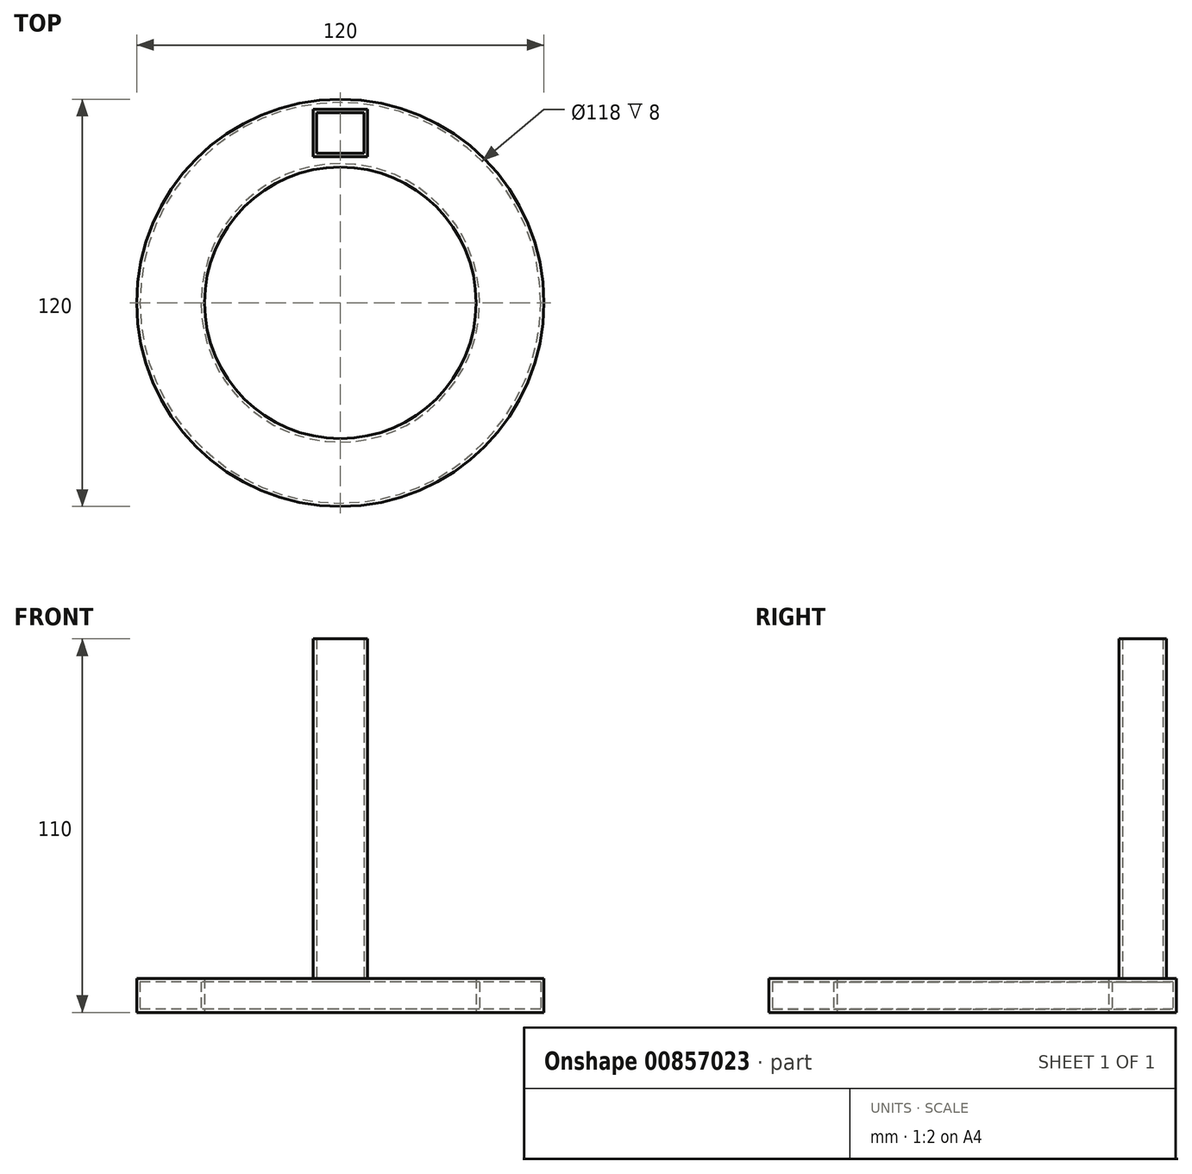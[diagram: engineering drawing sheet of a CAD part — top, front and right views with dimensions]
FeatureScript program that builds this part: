
annotation { "Feature Type Name" : "Feature", "Feature Type Description" : "" }
export const myFeature = defineFeature(function(context is Context, id is Id, definition is map)
    precondition{}
    {
        {
            var Q0;
            Q0=qCreatedBy(makeId("Top.planeOp"),FACE);
            var sketch = newSketch(context, id + "F0", { "sketchPlane" : qUnion([Q0])});
            skCircle(sketch, "E0", {"center": v(0, 0) * mm, "radius": 60 * mm});
            skSolve(sketch);
        }
        {
            var Q0;
            Q0=makeQuery(id+"F0.imprint","IMPRINT",FACE,{"disambiguationData":[TD([[makeQuery(id+"F0.imprint","IMPRINT",EDGE,{"derivedFrom":sQuery(id+"F0.wireOp",EDGE,"E0")}),1.0]])]});
            extrude(context, id + "F1", {"entities" : qUnion([Q0]), "depth" : 10 * mm, "offsetDistance" : 25 * mm});
        }
        {
            var Q0;
            Q0=qCreatedBy(makeId("Top.planeOp"),FACE);
            var sketch = newSketch(context, id + "F2", { "sketchPlane" : qUnion([Q0])});
            skCircle(sketch, "E1", {"center": v(0, 0) * mm, "radius": 40 * mm});
            skSolve(sketch);
        }
        {
            var Q0;
            Q0 = qSketchRegion(id + "F2", true);
            extrude(context, id + "F3", {"entities" : qUnion([Q0]), "operationType" : NewBodyOperationType.REMOVE, "depth" : 10 * mm, "offsetDistance" : 25 * mm});
        }
        {
            var Q0;
            Q0=makeQuery(id+"F1.opExtrude","CAP_FACE",FACE,{"disambiguationData":[OSD([sQuery(id+"F0.wireOp",EDGE,"E0")])],"isStart":false});
            var sketch = newSketch(context, id + "F4", { "sketchPlane" : qUnion([Q0])});
            skLineSegment(sketch, "E2.bottom", {"start": v(8, 43.05) * mm, "end": v(-8, 43.05) * mm});
            skLineSegment(sketch, "E2.top", {"start": v(8, 57.05) * mm, "end": v(-8, 57.05) * mm});
            skLineSegment(sketch, "E2.left", {"start": v(8, 43.05) * mm, "end": v(8, 57.05) * mm});
            skLineSegment(sketch, "E2.right", {"start": v(-8, 43.05) * mm, "end": v(-8, 57.05) * mm});
            skPoint(sketch, "E2.middle", {"position": v(0, 50.05) * mm});
            skSolve(sketch);
        }
        {
            var Q0;
            Q0 = qSketchRegion(id + "F4", true);
            extrude(context, id + "F5", {"entities" : qUnion([Q0]), "operationType" : NewBodyOperationType.ADD, "depth" : 100 * mm, "offsetDistance" : 25 * mm});
        }
        {
            var Q0;
            Q0=makeQuery(id+"F5.opExtrude","CAP_FACE",FACE,{"disambiguationData":[OSD([sQuery(id+"F4.wireOp",EDGE,"E2.bottom"),sQuery(id+"F4.wireOp",EDGE,"E2.top"),sQuery(id+"F4.wireOp",EDGE,"E2.left"),sQuery(id+"F4.wireOp",EDGE,"E2.right")])],"isStart":false});
            shell(context, id + "F6", {"entities" : qUnion([Q0]), "thickness" : 1 * mm});
        }
    });
